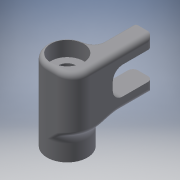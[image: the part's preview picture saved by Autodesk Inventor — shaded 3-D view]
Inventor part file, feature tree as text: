
AUTODESK INVENTOR PART (.ipt)
format: ipt  version: 2016 (Build 200138000, 138)  size: 269,824 bytes
history: native  units: mm
features: extrude x5, fillet x4, sketch x4, projected_geometry x1
ambient origin geometry x8: Origin, YZ Plane, XZ Plane, XY Plane, X Axis, Y Axis, Z Axis, Center Point
bodies: Body1 (feature_tree)
feature tree (14):
  extrude  "Extrusion7"  Depth=8.0mm
  extrude  "Extrusion12"  Depth=1.25mm
  extrude  "Extrusion13"  Depth=6.0mm TaperAngle=0.0deg
  extrude  "Extrusion14"  Depth=3.0mm TaperAngle=0.0deg
  extrude  "Extrusion16"  Depth=3.5mm
  fillet  "Fillet14"  Radius=11.0mm
  fillet  "Fillet5"  Radius=6.0mm
  fillet  "Fillet9"  Radius=5.0mm
  fillet  "Fillet10"  Radius=2.76mm
  sketch  "Sketch10"  dims[d51=8.0mm d52=8.0mm]
  sketch  "Sketch15"  dims[d53=4.0mm d56=1.25mm]
  sketch  "Sketch16"  dims[d57=10.0mm d58=0.0mm d69=6.0mm d70=0.0mm]
  sketch  "Sketch17"  dims[d71=6.5mm d72=3.0mm d73=0.0mm d74=3.5mm d75=11.0mm d76=0.0mm d79=6.0mm d80=5.0mm d83=2.76mm d87=3.26mm d88=1.0mm d99=10.0mm d100=0.0mm d103=2.0mm]
  projected_geometry  "Projected Loop10"
